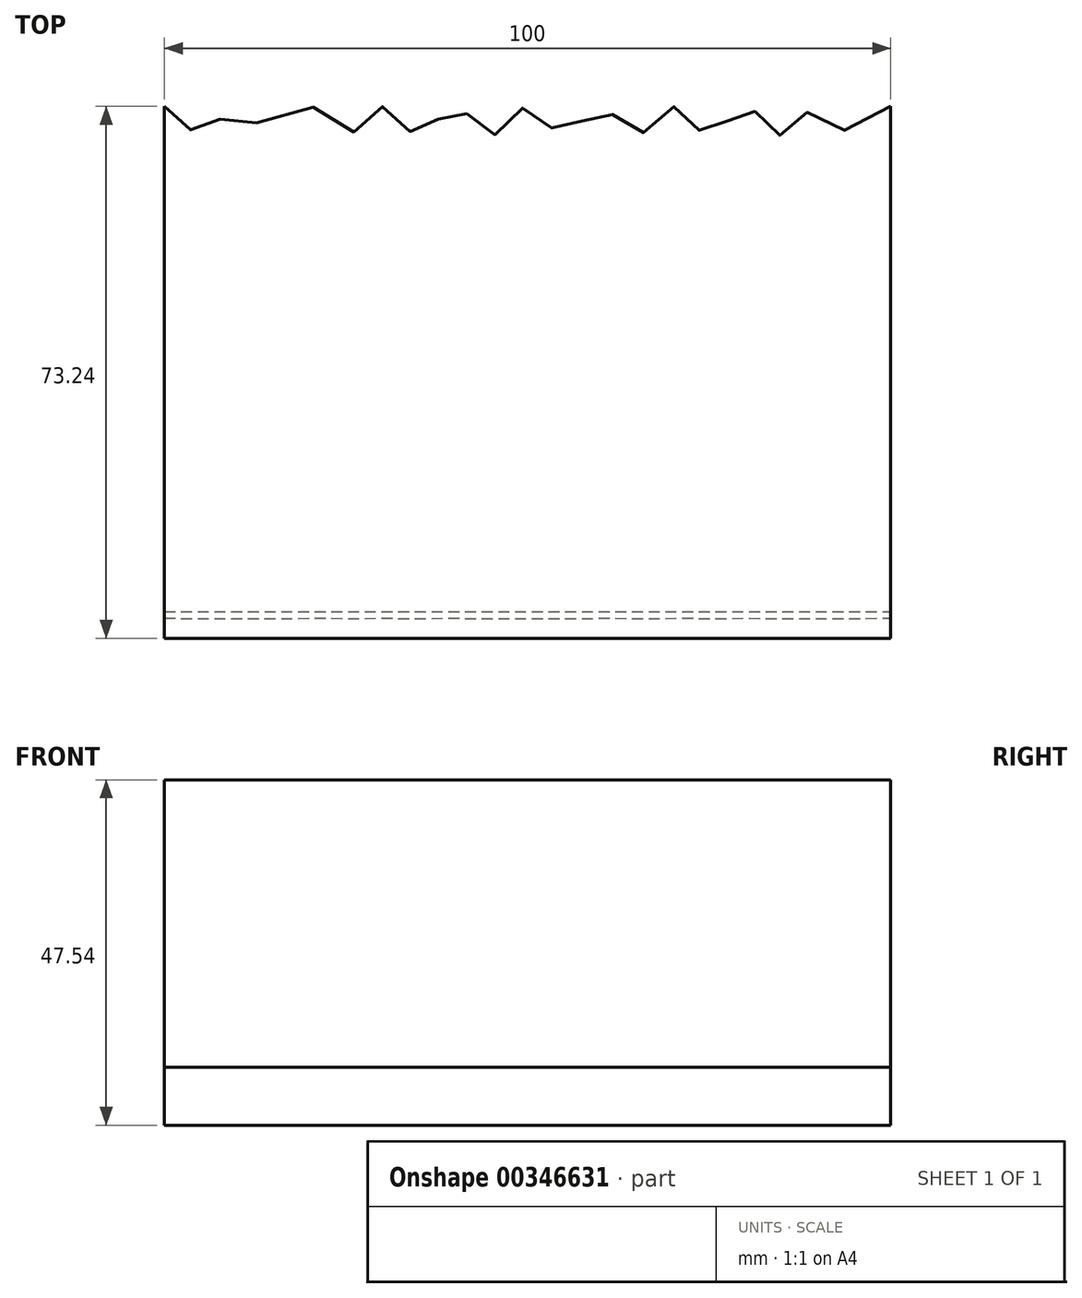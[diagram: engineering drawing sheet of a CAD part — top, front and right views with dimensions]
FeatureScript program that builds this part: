
annotation { "Feature Type Name" : "Feature", "Feature Type Description" : "" }
export const myFeature = defineFeature(function(context is Context, id is Id, definition is map)
    precondition{}
    {
        {
            var Q0;
            Q0=qCreatedBy(makeId("Right.planeOp"),FACE);
            var sketch = newSketch(context, id + "F0", { "sketchPlane" : qUnion([Q0])});
            skPoint(sketch, "E0", {"position": v(-15, 0) * mm});
            skLineSegment(sketch, "E1", {"start": v(-15, 0) * mm, "end": v(-71.3, -32.5) * mm, "construction": true});
            skEllipse(sketch, "E2", {"center": v(-15, 0) * mm, "majorRadius": 15 * mm, "minorRadius": 7 * mm, "majorAxis": v(1, 0)});
            skPoint(sketch, "E3", {"position": v(0, 0) * mm});
            skPoint(sketch, "E4", {"position": v(-15, 7) * mm});
            skLineSegment(sketch, "E5", {"start": v(-70.54, -33.8) * mm, "end": v(-72.04, -31.2) * mm, "construction": true});
            skPoint(sketch, "E6", {"position": v(-71.3, -32.5) * mm});
            skArc(sketch, "E7", {"start": v(-8.64, -6.34) * mm, "mid": v(-40.7, -16.8) * mm, "end": v(-70.04, -33.44) * mm});
            skArc(sketch, "E8", {"start": v(-26.32, 4.6) * mm, "mid": v(-51.43, -11.9) * mm, "end": v(-73.24, -32.54) * mm});
            skPoint(sketch, "E9", {"position": v(-72.04, -31.2) * mm});
            skLineSegment(sketch, "E10", {"start": v(-70.45, -34.4) * mm, "end": v(-69.56, -40.54) * mm});
            skLineSegment(sketch, "E11", {"start": v(-69.56, -40.54) * mm, "end": v(-73.24, -32.54) * mm});
            skPoint(sketch, "E12.visualSharp", {"position": v(-70.54, -33.8) * mm});
            skArc(sketch, "E12.filletArc", {"start": v(-70.04, -33.44) * mm, "mid": v(-70.38, -33.87) * mm, "end": v(-70.45, -34.4) * mm});
            skLineSegment(sketch, "E13", {"start": v(-15, 0) * mm, "end": v(-30, 0) * mm, "construction": true});
            skSolve(sketch);
        }
        {
            var Q0;
            Q0=qCreatedBy(makeId("Right.planeOp"),FACE);
            cPlane(context, id + "F1", {"entities" : qUnion([Q0]), "cplaneType" : CPlaneType.OFFSET, "offset" : 100 * mm, "width" : 150 * mm, "height" : 150 * mm});
        }
        {
            var Q0;
            Q0=qCreatedBy(id+"F1.planeOp",FACE);
            var sketch = newSketch(context, id + "F2", { "sketchPlane" : qUnion([Q0])});
            skPoint(sketch, "E14", {"position": v(-15, 0) * mm});
            skLineSegment(sketch, "E15", {"start": v(-15, 0) * mm, "end": v(-71.3, -32.5) * mm, "construction": true});
            skEllipse(sketch, "E16", {"center": v(-15, 0) * mm, "majorRadius": 15 * mm, "minorRadius": 7 * mm, "majorAxis": v(1, 0)});
            skPoint(sketch, "E17", {"position": v(0, 0) * mm});
            skPoint(sketch, "E18", {"position": v(-15, 7) * mm});
            skLineSegment(sketch, "E19", {"start": v(-70.54, -33.8) * mm, "end": v(-72.04, -31.2) * mm, "construction": true});
            skPoint(sketch, "E20", {"position": v(-71.3, -32.5) * mm});
            skArc(sketch, "E21", {"start": v(-8.64, -6.34) * mm, "mid": v(-40.7, -16.8) * mm, "end": v(-70.04, -33.44) * mm});
            skArc(sketch, "E22", {"start": v(-26.32, 4.6) * mm, "mid": v(-51.43, -11.9) * mm, "end": v(-73.24, -32.54) * mm});
            skPoint(sketch, "E23", {"position": v(-72.04, -31.2) * mm});
            skLineSegment(sketch, "E24", {"start": v(-70.45, -34.4) * mm, "end": v(-69.56, -40.54) * mm});
            skLineSegment(sketch, "E25", {"start": v(-69.56, -40.54) * mm, "end": v(-73.24, -32.54) * mm});
            skPoint(sketch, "E26.visualSharp", {"position": v(-70.54, -33.8) * mm});
            skArc(sketch, "E26.filletArc", {"start": v(-70.04, -33.44) * mm, "mid": v(-70.38, -33.87) * mm, "end": v(-70.45, -34.4) * mm});
            skLineSegment(sketch, "E27", {"start": v(-15, 0) * mm, "end": v(-30, 0) * mm, "construction": true});
            skSolve(sketch);
        }
        {
            var Q0;
            Q0=qCreatedBy(makeId("Top.planeOp"),FACE);
            var sketch = newSketch(context, id + "F3", { "sketchPlane" : qUnion([Q0])});
            skPoint(sketch, "E28", {"position": v(100, 0) * mm});
            skPoint(sketch, "E29", {"position": v(10, 0) * mm});
            skPoint(sketch, "E30", {"position": v(20, 0) * mm});
            skPoint(sketch, "E31", {"position": v(30, 0) * mm});
            skPoint(sketch, "E32", {"position": v(40, 0) * mm});
            skPoint(sketch, "E33", {"position": v(50, 0) * mm});
            skPoint(sketch, "E34", {"position": v(60, 0) * mm});
            skPoint(sketch, "E35", {"position": v(70, 0) * mm});
            skPoint(sketch, "E36", {"position": v(80, 0) * mm});
            skPoint(sketch, "E37", {"position": v(90, 0) * mm});
            skLineSegment(sketch, "E38", {"start": v(0, 0) * mm, "end": v(10, 0) * mm, "construction": true});
            skLineSegment(sketch, "E39", {"start": v(10, 0) * mm, "end": v(20, 0) * mm, "construction": true});
            skLineSegment(sketch, "E40", {"start": v(20, 0) * mm, "end": v(30, 0) * mm, "construction": true});
            skLineSegment(sketch, "E41", {"start": v(30, 0) * mm, "end": v(40, 0) * mm, "construction": true});
            skLineSegment(sketch, "E42", {"start": v(40, 0) * mm, "end": v(50, 0) * mm, "construction": true});
            skLineSegment(sketch, "E43", {"start": v(50, 0) * mm, "end": v(60, 0) * mm, "construction": true});
            skLineSegment(sketch, "E44", {"start": v(60, 0) * mm, "end": v(70, 0) * mm, "construction": true});
            skLineSegment(sketch, "E45", {"start": v(70, 0) * mm, "end": v(80, 0) * mm, "construction": true});
            skLineSegment(sketch, "E46", {"start": v(80, 0) * mm, "end": v(90, 0) * mm, "construction": true});
            skLineSegment(sketch, "E47", {"start": v(90, 0) * mm, "end": v(100, 0) * mm, "construction": true});
            skPoint(sketch, "E48", {"position": v(5, -4) * mm});
            skPoint(sketch, "E48.positionSnap0", {"position": v(5, 0) * mm});
            skPoint(sketch, "E49", {"position": v(15, -4) * mm});
            skPoint(sketch, "E49.positionSnap0", {"position": v(15, 0) * mm});
            skPoint(sketch, "E50", {"position": v(25, -4) * mm});
            skPoint(sketch, "E50.positionSnap0", {"position": v(25, 0) * mm});
            skPoint(sketch, "E51", {"position": v(35, -4) * mm});
            skPoint(sketch, "E51.positionSnap0", {"position": v(35, 0) * mm});
            skPoint(sketch, "E52", {"position": v(45, -4) * mm});
            skPoint(sketch, "E52.positionSnap0", {"position": v(45, 0) * mm});
            skPoint(sketch, "E53", {"position": v(55, -4) * mm});
            skPoint(sketch, "E53.positionSnap0", {"position": v(55, 0) * mm});
            skPoint(sketch, "E54", {"position": v(65, -4) * mm});
            skPoint(sketch, "E54.positionSnap0", {"position": v(65, 0) * mm});
            skPoint(sketch, "E55", {"position": v(75, -4) * mm});
            skPoint(sketch, "E55.positionSnap0", {"position": v(75, 0) * mm});
            skPoint(sketch, "E56", {"position": v(85, -4) * mm});
            skPoint(sketch, "E56.positionSnap0", {"position": v(85, 0) * mm});
            skPoint(sketch, "E57", {"position": v(95, -4) * mm});
            skPoint(sketch, "E57.positionSnap0", {"position": v(95, 0) * mm});
            skFitSpline(sketch, "E58", {"points": [v(0, 0) * mm, v(5, -4) * mm, v(10, 0) * mm, v(15, -4) * mm, v(20, 0) * mm, v(25, -4) * mm, v(30, 0) * mm, v(35, -4) * mm, v(40, 0) * mm, v(45, -4) * mm, v(50, 0) * mm, v(55, -4) * mm, v(60, 0) * mm, v(65, -4) * mm, v(70, 0) * mm, v(75, -4) * mm, v(80, 0) * mm, v(85, -4) * mm, v(90, 0) * mm, v(95, -4) * mm, v(100, 0) * mm], "startDerivative": vector(100, 0) * mm, "endDerivative": vector(100, 0) * mm});
            skPoint(sketch, "E59", {"position": v(97.5, -2) * mm});
            skPoint(sketch, "E60", {"position": v(92.5, -2) * mm});
            skPoint(sketch, "E61", {"position": v(87.5, -2) * mm});
            skPoint(sketch, "E62", {"position": v(82.5, -2) * mm});
            skPoint(sketch, "E63", {"position": v(77.5, -2) * mm});
            skPoint(sketch, "E64", {"position": v(72.5, -2) * mm});
            skPoint(sketch, "E65", {"position": v(67.5, -2) * mm});
            skPoint(sketch, "E66", {"position": v(62.5, -2) * mm});
            skPoint(sketch, "E67", {"position": v(57.5, -2) * mm});
            skPoint(sketch, "E68", {"position": v(52.5, -2) * mm});
            skPoint(sketch, "E69", {"position": v(47.5, -2) * mm});
            skPoint(sketch, "E70", {"position": v(42.5, -2) * mm});
            skPoint(sketch, "E71", {"position": v(37.5, -2) * mm});
            skPoint(sketch, "E72", {"position": v(32.5, -2) * mm});
            skPoint(sketch, "E73", {"position": v(27.5, -2) * mm});
            skPoint(sketch, "E74", {"position": v(22.5, -2) * mm});
            skPoint(sketch, "E75", {"position": v(17.5, -2) * mm});
            skPoint(sketch, "E76", {"position": v(12.5, -2) * mm});
            skPoint(sketch, "E77", {"position": v(7.5, -2) * mm});
            skPoint(sketch, "E78", {"position": v(2.5, -2) * mm});
            skSolve(sketch);
        }
        {
            var Q0;
            Q0=sQuery(id+"F3.wireOp",EDGE,"E58");
            var Q1;
            Q1 = qSketchRegion(id + "F0", true);
            var Q2;
            Q2 = qSketchRegion(id + "F2", true);
            var Q3;
            Q3=sQuery(id+"F3.wireOp",EDGE,"E58");
            loft(context, id + "F4", {"spine" : qUnion([Q0]), "addGuides" : true, "sheetProfilesArray" : [{ "sheetProfileEntities" : qUnion([Q1]) }, { "sheetProfileEntities" : qUnion([Q2]) }], "guidesArray" : [{ "guideEntities" : qUnion([Q3]), "guideDerivativeType" : LoftGuideDerivativeType.DEFAULT, "guideDerivativeMagnitude" : 1 }]});
        }
    });
